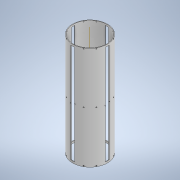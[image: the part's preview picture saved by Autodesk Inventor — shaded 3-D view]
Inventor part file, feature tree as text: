
AUTODESK INVENTOR PART (.ipt)
format: ipt  version: 2021 (Build 250183000, 183)  size: 339,968 bytes
history: native  units: in
note: dims shown in document units (in); Inventor stores cm internally (conversion verified against a paired STEP export)
features: other x26, pattern_circular x6, hole x6, sketch x5, plane x3, extrude x2
ambient origin geometry x8: Origin, YZ Plane, XZ Plane, XY Plane, X Axis, Y Axis, Z Axis, Center Point
bodies: Solid1 (feature_tree)
feature tree (48):
  extrude  "Extrusion1"  Depth=0.3937in
  plane  "Work Plane1"
  extrude  "Extrusion2"  Depth=1.5748in TaperAngle=360.0deg
  pattern_circular  "Circular Pattern1"  [2 undecoded]
  other  "Work Axis1"
  other  "Work Axis2"
  other  "Work Axis3"
  other  "Work Axis4"
  other  "Work Point1"
  other  "Work Point2"
  other  "Work Point3"
  other  "Central Plane"
  other  "Work Point4"
  other  "Work Axis6"
  other  "Work Axis7"
  other  "Offset Plane A"
  other  "Work Point5"
  other  "Work Point6"
  other  "Work Axis8"
  other  "Work Axis9"
  other  "Work Point7"
  other  "Work Point8"
  plane  "Work Plane5"
  plane  "Work Plane6"
  hole  "Hole1"  [1 undecoded]
  hole  "Hole2"  [1 undecoded]
  pattern_circular  "Circular Pattern3"  Angle=30.0deg  [1 undecoded]
  sketch  "Sketch5"  dims[d13=0.0481in]
  other  "Work Axis10"
  other  "plane for insert hole 1"
  sketch  "Sketch7"  dims[d14=-11.811in]
  other  "plane for insert hole 2"
  sketch  "Sketch8"  dims[d15=0.0481in d16=0.1574in d17=-0.1574in d48=1.0in d49=1.0in d29=0.096in d30=0.75in d31=0.185in d32=0.25in d33=0.5635in d34=1.0in d35=0.0in d52=1.0in d53=1.0in d38=0.096in d39=0.75in d40=0.185in d41=0.25in d42=0.5635in d43=1.0in d44=0.8108in d45=1.5748in d46=360.0deg d88=30.0deg d89=30.0deg d90=0.0in d91=0.0in d92=0.0in d93=11.811in d94=0.0in d95=11.811in d96=0.129in d97=0.224in d98=0.225in d99=0.25in d100=0.5635in d101=0.349in d102=0.8108in d103=0.129in d104=0.224in d105=0.225in d106=0.25in d107=0.5635in d108=0.349in d109=0.8108in d110=1.5748in d111=360.0deg d116=1.5748in d117=360.0deg d119=0.0in d120=0.0in d121=0.0in d122=0.1969in d123=0.1969in d124=0.0in d125=0.0in d126=0.1969in d127=0.1969in d128=0.129in d129=0.75in d130=0.225in d131=0.25in d132=0.5635in d133=0.349in d134=0.8108in d135=0.129in d136=0.75in d137=0.225in d138=0.25in d139=0.5635in d140=0.349in d141=0.8108in d142=1.5748in d143=360.0deg d145=1.5748in d146=360.0deg d148=22.8346in d149=-0.1969in d150=-0.1969in d54=1.0in d55=1.0in d56=1.0in d57=0.15in d58=0.25in d59=0.375in d60=0.5635in d61=0.75in d62=0.8108in d63=0.0625in d64=0.75in d65=0.375in]
  hole  "insert hole 2"  [1 undecoded]
  hole  "insert hole 1"  [1 undecoded]
  pattern_circular  "Circular Pattern7"  [2 undecoded]
  pattern_circular  "Circular Pattern9"  [2 undecoded]
  other  "Work Axis14"
  hole  "Hole8"  [1 undecoded]
  hole  "Hole9"  [1 undecoded]
  pattern_circular  "Circular Pattern10"  Count=30  [1 undecoded]
  pattern_circular  "Circular Pattern11"  Count=4 Angle=360.0deg
  other  "Edge Hole Plane 1"
  other  "Edge Hole Plane 2"
  sketch  "Sketch1"  dims[d3=0.0in d7=0.3937in]
  sketch  "Sketch2"  dims[d8=0.5in d9=0.0in d10=1.5748in d11=360.0deg]
  other  "Work Axis5"
  other  "Offset Plane B"
note: 14 required parameter values undecoded (feature->parameter linkage not recoverable at this tier; creation-order binding heuristic only, values carry confidence <= 0.55)
